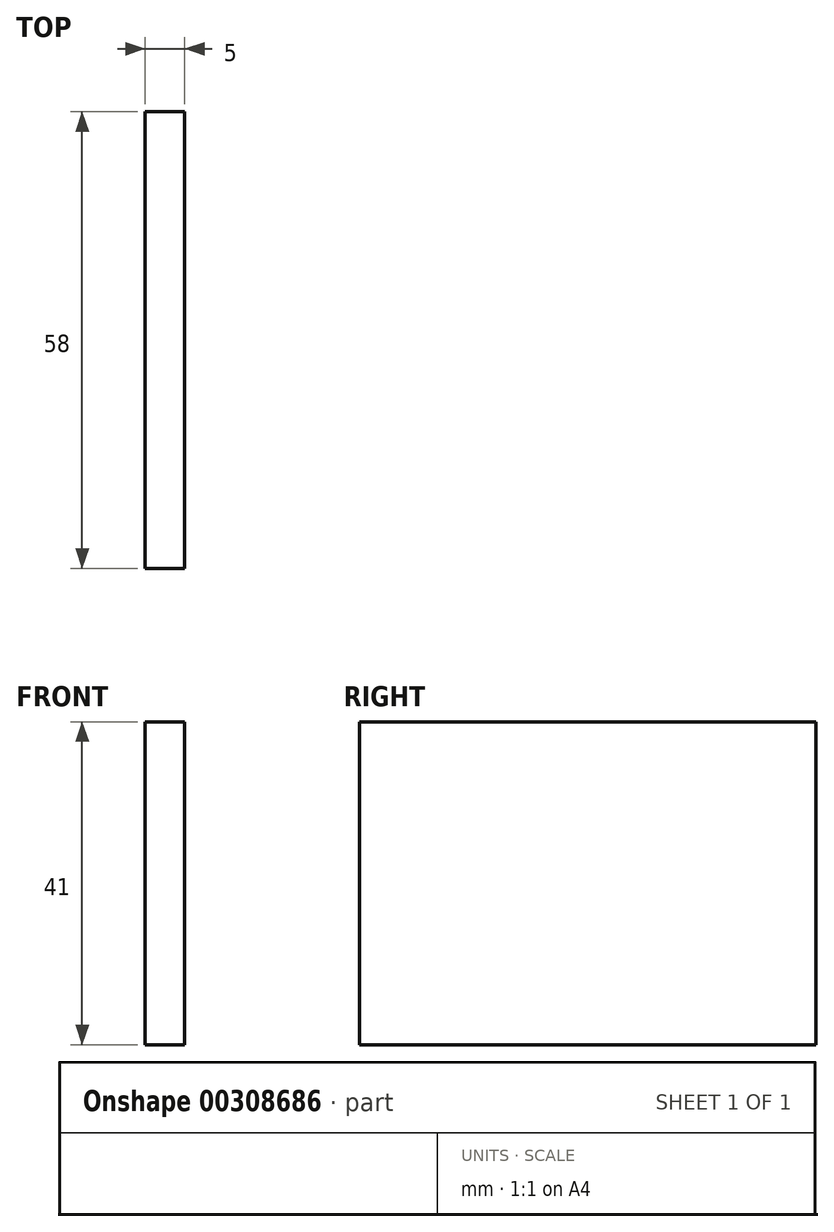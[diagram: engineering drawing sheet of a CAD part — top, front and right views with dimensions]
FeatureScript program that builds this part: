
annotation { "Feature Type Name" : "Feature", "Feature Type Description" : "" }
export const myFeature = defineFeature(function(context is Context, id is Id, definition is map)
    precondition{}
    {
        {
            var Q0;
            Q0=qCreatedBy(makeId("Front.planeOp"),FACE);
            var sketch = newSketch(context, id + "F0", { "sketchPlane" : qUnion([Q0])});
            skLineSegment(sketch, "E0.bottom", {"start": v(2.5, 20.5) * mm, "end": v(-2.5, 20.5) * mm});
            skLineSegment(sketch, "E0.top", {"start": v(2.5, -20.5) * mm, "end": v(-2.5, -20.5) * mm});
            skLineSegment(sketch, "E0.left", {"start": v(2.5, 20.5) * mm, "end": v(2.5, -20.5) * mm});
            skLineSegment(sketch, "E0.right", {"start": v(-2.5, 20.5) * mm, "end": v(-2.5, -20.5) * mm});
            skPoint(sketch, "E0.middle", {"position": v(0, 0) * mm});
            skSolve(sketch);
        }
        {
            var Q0;
            Q0 = qSketchRegion(id + "F0", true);
            extrude(context, id + "F1", {"entities" : qUnion([Q0]), "depth" : 58 * mm});
        }
    });
